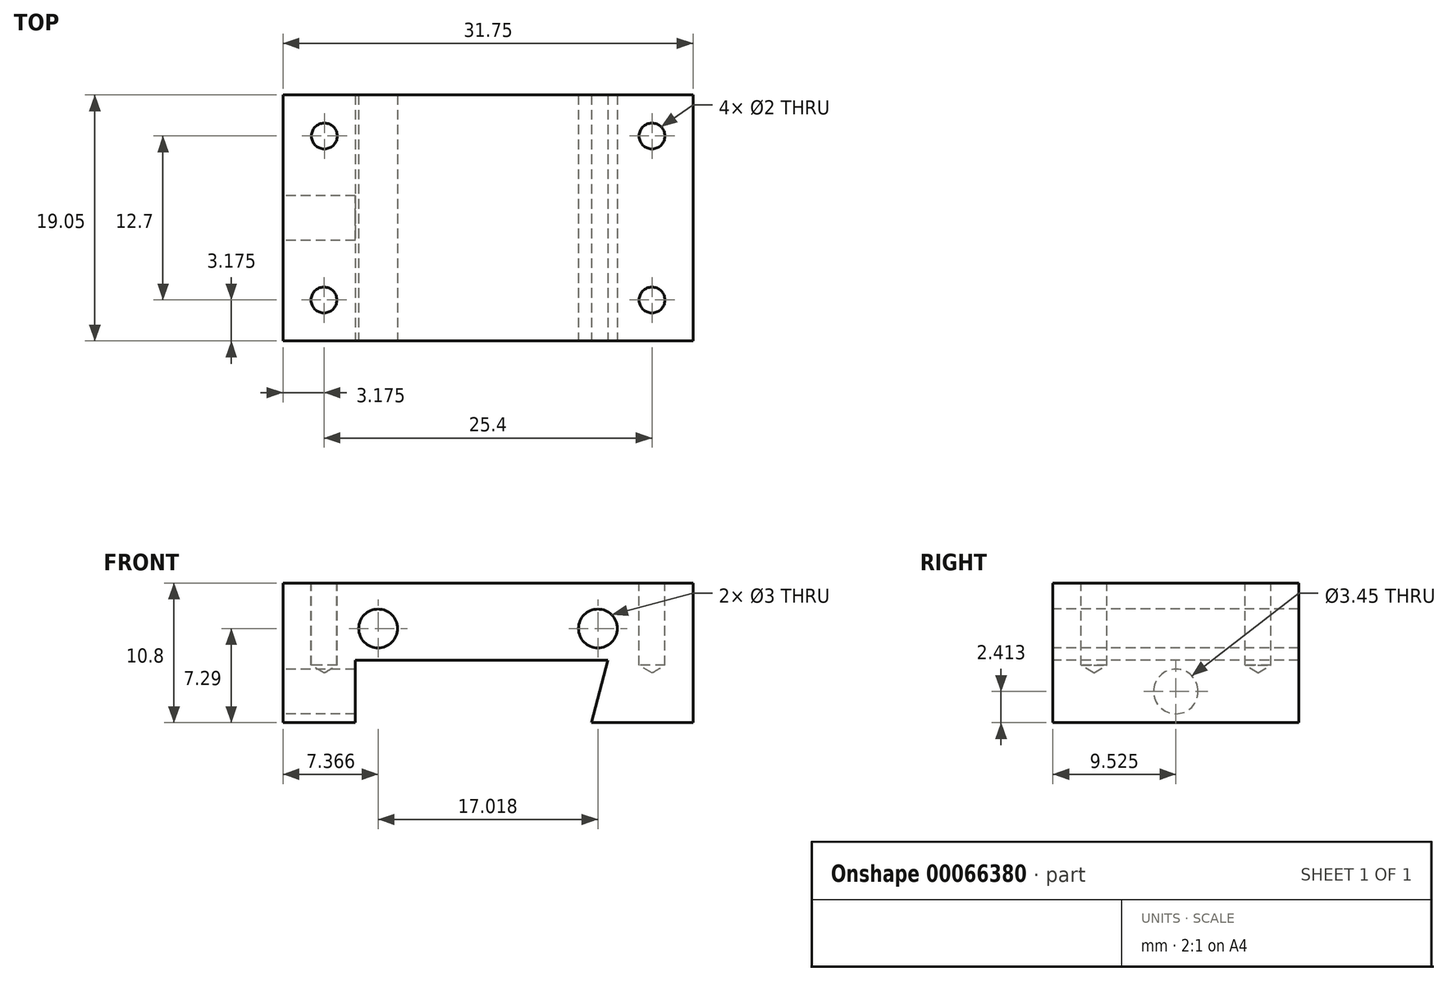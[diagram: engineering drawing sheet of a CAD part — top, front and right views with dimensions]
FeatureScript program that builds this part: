
annotation { "Feature Type Name" : "Feature", "Feature Type Description" : "" }
export const myFeature = defineFeature(function(context is Context, id is Id, definition is map)
    precondition{}
    {
        {
            var Q0;
            Q0=qCreatedBy(makeId("Top.planeOp"),FACE);
            var sketch = newSketch(context, id + "F0", { "sketchPlane" : qUnion([Q0])});
            skLineSegment(sketch, "E0.bottom", {"start": v(0, 0) * mm, "end": v(31.75, 0) * mm});
            skLineSegment(sketch, "E0.top", {"start": v(0, 19.05) * mm, "end": v(31.75, 19.05) * mm});
            skLineSegment(sketch, "E0.left", {"start": v(0, 0) * mm, "end": v(0, 19.05) * mm});
            skLineSegment(sketch, "E0.right", {"start": v(31.75, 0) * mm, "end": v(31.75, 19.05) * mm});
            skSolve(sketch);
        }
        {
            var Q0;
            Q0 = qSketchRegion(id + "F0", true);
            extrude(context, id + "F1", {"entities" : qUnion([Q0]), "depth" : 10.8 * mm});
        }
        {
            var Q0;
            Q0=makeQuery(id+"F1.opExtrude","SWEPT_FACE",FACE,{"disambiguationData":[OSD([sQuery(id+"F0.wireOp",EDGE,"E0.bottom")])]});
            var sketch = newSketch(context, id + "F2", { "sketchPlane" : qUnion([Q0])});
            skLineSegment(sketch, "E1", {"start": v(25.17, 4.83) * mm, "end": v(5.59, 4.83) * mm});
            skLineSegment(sketch, "E2", {"start": v(5.59, 4.83) * mm, "end": v(5.59, 0) * mm});
            skLineSegment(sketch, "E3", {"start": v(25.17, 4.83) * mm, "end": v(23.88, 0) * mm});
            skLineSegment(sketch, "E4", {"start": v(5.59, 0) * mm, "end": v(23.88, 0) * mm});
            skSolve(sketch);
        }
        {
            var Q0;
            Q0 = qSketchRegion(id + "F2", true);
            extrude(context, id + "F3", {"entities" : qUnion([Q0]), "operationType" : NewBodyOperationType.REMOVE, "oppositeDirection" : true, "depth" : 25.4 * mm});
        }
        {
            var Q0;
            Q0=makeQuery(id+"F1.opExtrude","SWEPT_FACE",FACE,{"disambiguationData":[OSD([sQuery(id+"F0.wireOp",EDGE,"E0.bottom")])]});
            var sketch = newSketch(context, id + "F4", { "sketchPlane" : qUnion([Q0])});
            skPoint(sketch, "E5", {"position": v(7.37, 7.29) * mm});
            skPoint(sketch, "E6", {"position": v(24.38, 7.29) * mm});
            skSolve(sketch);
        }
        {
            var Q0;
            Q0=sQuery(id+"F4.wireOp",VERTEX,"E5");
            var Q1;
            Q1=sQuery(id+"F4.wireOp",VERTEX,"E6");
            var Q2;
            Q2=makeQuery(id+"F1.opExtrude","SWEPT_BODY",BODY,{"disambiguationData":[OSD([sQuery(id+"F0.wireOp",EDGE,"E0.bottom"),sQuery(id+"F0.wireOp",EDGE,"E0.top"),sQuery(id+"F0.wireOp",EDGE,"E0.left"),sQuery(id+"F0.wireOp",EDGE,"E0.right")])]});
            hole(context, id + "F5", {"style" : HoleStyle.SIMPLE, "holeDiameter" : 3 * mm, "endStyle" : HoleEndStyle.THROUGH, "locations" : qUnion([Q0, Q1]), "scope" : qUnion([Q2])});
        }
        {
            var Q0;
            Q0=makeQuery(id+"F1.opExtrude","CAP_FACE",FACE,{"disambiguationData":[OSD([sQuery(id+"F0.wireOp",EDGE,"E0.bottom"),sQuery(id+"F0.wireOp",EDGE,"E0.top"),sQuery(id+"F0.wireOp",EDGE,"E0.left"),sQuery(id+"F0.wireOp",EDGE,"E0.right")])],"isStart":false});
            var sketch = newSketch(context, id + "F6", { "sketchPlane" : qUnion([Q0])});
            skPoint(sketch, "E7", {"position": v(3.2, 15.88) * mm});
            skPoint(sketch, "E8", {"position": v(3.18, 3.18) * mm});
            skPoint(sketch, "E9", {"position": v(28.57, 15.88) * mm});
            skPoint(sketch, "E10", {"position": v(28.57, 3.18) * mm});
            skSolve(sketch);
        }
        {
            var Q0;
            Q0=sQuery(id+"F6.wireOp",VERTEX,"E7");
            var Q1;
            Q1=sQuery(id+"F6.wireOp",VERTEX,"E8");
            var Q2;
            Q2=sQuery(id+"F6.wireOp",VERTEX,"E9");
            var Q3;
            Q3=sQuery(id+"F6.wireOp",VERTEX,"E10");
            var Q4;
            Q4=makeQuery(id+"F1.opExtrude","SWEPT_BODY",BODY,{"disambiguationData":[OSD([sQuery(id+"F0.wireOp",EDGE,"E0.bottom"),sQuery(id+"F0.wireOp",EDGE,"E0.top"),sQuery(id+"F0.wireOp",EDGE,"E0.left"),sQuery(id+"F0.wireOp",EDGE,"E0.right")])]});
            hole(context, id + "F7", {"style" : HoleStyle.SIMPLE, "holeDiameter" : 2 * mm, "endStyle" : HoleEndStyle.BLIND, "holeDepth" : 6.35 * mm, "locations" : qUnion([Q0, Q1, Q2, Q3]), "scope" : qUnion([Q4])});
        }
        {
            var Q0;
            Q0=makeQuery(id+"F1.opExtrude","SWEPT_FACE",FACE,{"disambiguationData":[OSD([sQuery(id+"F0.wireOp",EDGE,"E0.left")])]});
            var sketch = newSketch(context, id + "F8", { "sketchPlane" : qUnion([Q0])});
            skPoint(sketch, "E11", {"position": v(-9.53, 2.41) * mm});
            skSolve(sketch);
        }
        {
            var Q0;
            Q0=sQuery(id+"F8.wireOp",VERTEX,"E11");
            var Q1;
            Q1=makeQuery(id+"F1.opExtrude","SWEPT_BODY",BODY,{"disambiguationData":[OSD([sQuery(id+"F0.wireOp",EDGE,"E0.bottom"),sQuery(id+"F0.wireOp",EDGE,"E0.top"),sQuery(id+"F0.wireOp",EDGE,"E0.left"),sQuery(id+"F0.wireOp",EDGE,"E0.right")])]});
            hole(context, id + "F9", {"style" : HoleStyle.SIMPLE, "holeDiameter" : 3.45 * mm, "endStyle" : HoleEndStyle.BLIND, "holeDepth" : 6.35 * mm, "locations" : qUnion([Q0]), "scope" : qUnion([Q1])});
        }
    });
